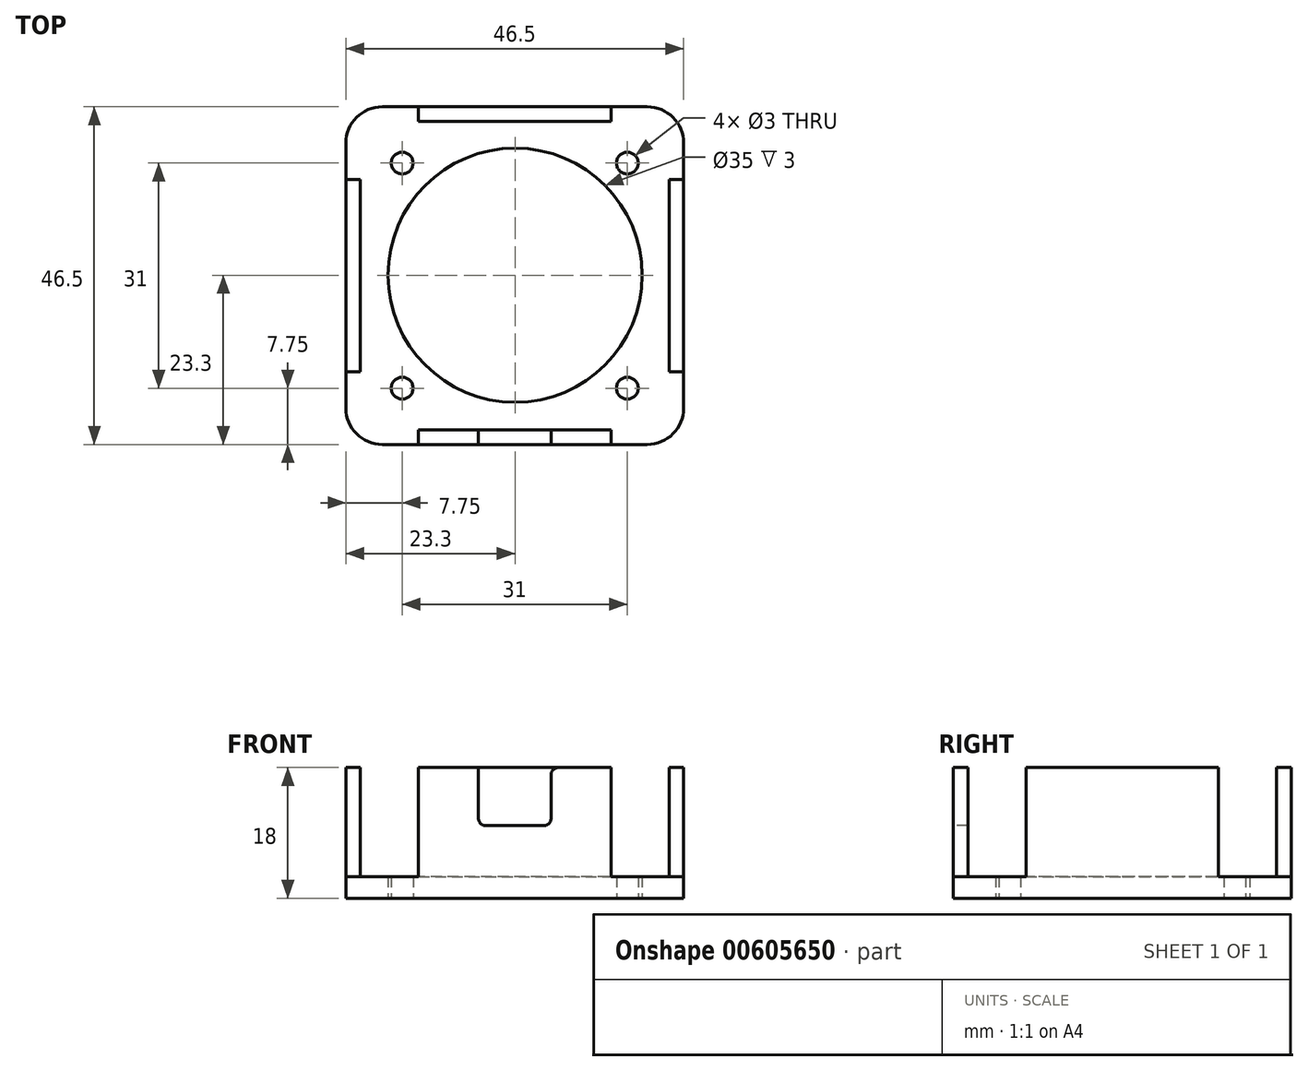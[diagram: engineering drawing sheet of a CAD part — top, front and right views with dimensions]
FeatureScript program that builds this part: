
annotation { "Feature Type Name" : "Feature", "Feature Type Description" : "" }
export const myFeature = defineFeature(function(context is Context, id is Id, definition is map)
    precondition{}
    {
        {
            var Q0;
            Q0=qCreatedBy(makeId("Top.planeOp"),FACE);
            var sketch = newSketch(context, id + "F0", { "sketchPlane" : qUnion([Q0])});
            skLineSegment(sketch, "E0.bottom", {"start": v(0, 0) * mm, "end": v(46.5, 0) * mm});
            skLineSegment(sketch, "E0.top", {"start": v(0, 46.5) * mm, "end": v(46.5, 46.5) * mm});
            skLineSegment(sketch, "E0.left", {"start": v(0, 0) * mm, "end": v(0, 46.5) * mm});
            skLineSegment(sketch, "E0.right", {"start": v(46.5, 0) * mm, "end": v(46.5, 46.5) * mm});
            skCircle(sketch, "E1", {"center": v(23.3, 23.3) * mm, "radius": 17.5 * mm});
            skCircle(sketch, "E2", {"center": v(7.75, 7.75) * mm, "radius": 1.5 * mm});
            skCircle(sketch, "E3", {"center": v(7.75, 38.75) * mm, "radius": 1.5 * mm});
            skCircle(sketch, "E4", {"center": v(38.75, 38.75) * mm, "radius": 1.5 * mm});
            skCircle(sketch, "E5", {"center": v(38.75, 7.75) * mm, "radius": 1.5 * mm});
            skSolve(sketch);
        }
        {
            var Q0;
            Q0 = qSketchRegion(id + "F0", true);
            extrude(context, id + "F1", {"entities" : qUnion([Q0]), "depth" : 3 * mm, "offsetDistance" : 25 * mm});
        }
        {
            var Q0;
            Q0=makeQuery(id+"F1.opExtrude","CAP_FACE",FACE,{"disambiguationData":[OSD([sQuery(id+"F0.wireOp",EDGE,"E0.bottom"),sQuery(id+"F0.wireOp",EDGE,"E0.top"),sQuery(id+"F0.wireOp",EDGE,"E0.left"),sQuery(id+"F0.wireOp",EDGE,"E0.right"),sQuery(id+"F0.wireOp",EDGE,"E1")])],"isStart":false});
            var sketch = newSketch(context, id + "F2", { "sketchPlane" : qUnion([Q0])});
            skLineSegment(sketch, "E6.bottom", {"start": v(0, 46.5) * mm, "end": v(2, 46.5) * mm});
            skLineSegment(sketch, "E6.top", {"start": v(0, 0) * mm, "end": v(2, 0) * mm});
            skLineSegment(sketch, "E6.left", {"start": v(0, 46.5) * mm, "end": v(0, 0) * mm});
            skLineSegment(sketch, "E6.right", {"start": v(2, 46.5) * mm, "end": v(2, 0) * mm});
            skLineSegment(sketch, "E7.bottom", {"start": v(44.5, 46.5) * mm, "end": v(46.5, 46.5) * mm});
            skLineSegment(sketch, "E7.top", {"start": v(44.5, 0) * mm, "end": v(46.5, 0) * mm});
            skLineSegment(sketch, "E7.left", {"start": v(44.5, 46.5) * mm, "end": v(44.5, 0) * mm});
            skLineSegment(sketch, "E7.right", {"start": v(46.5, 46.5) * mm, "end": v(46.5, 0) * mm});
            skLineSegment(sketch, "E8.bottom", {"start": v(2, 46.5) * mm, "end": v(44.5, 46.5) * mm});
            skLineSegment(sketch, "E8.top", {"start": v(2, 44.5) * mm, "end": v(44.5, 44.5) * mm});
            skLineSegment(sketch, "E8.left", {"start": v(2, 46.5) * mm, "end": v(2, 44.5) * mm});
            skLineSegment(sketch, "E8.right", {"start": v(44.5, 46.5) * mm, "end": v(44.5, 44.5) * mm});
            skLineSegment(sketch, "E9.bottom", {"start": v(2, 0) * mm, "end": v(44.5, 0) * mm});
            skLineSegment(sketch, "E9.top", {"start": v(2, 2) * mm, "end": v(44.5, 2) * mm});
            skLineSegment(sketch, "E9.left", {"start": v(2, 0) * mm, "end": v(2, 2) * mm});
            skLineSegment(sketch, "E9.right", {"start": v(44.5, 0) * mm, "end": v(44.5, 2) * mm});
            skSolve(sketch);
        }
        {
            var Q0;
            Q0 = qSketchRegion(id + "F2", true);
            extrude(context, id + "F3", {"entities" : qUnion([Q0]), "operationType" : NewBodyOperationType.ADD, "depth" : 15 * mm, "offsetDistance" : 25 * mm});
        }
        {
            var Q0;
            Q0=makeQuery(id+"F3.boolean.opBoolean","MERGE",FACE,{"derivedFrom":[makeQuery(id+"F1.opExtrude","SWEPT_FACE",FACE,{"disambiguationData":[OSD([sQuery(id+"F0.wireOp",EDGE,"E0.bottom")])]}),makeQuery(id+"F3.opExtrude","SWEPT_FACE",FACE,{"disambiguationData":[OSD([sQuery(id+"F2.wireOp",EDGE,"E6.top"),sQuery(id+"F2.wireOp",EDGE,"E7.top"),sQuery(id+"F2.wireOp",EDGE,"E9.bottom")])]})]});
            var sketch = newSketch(context, id + "F4", { "sketchPlane" : qUnion([Q0])});
            skLineSegment(sketch, "E10.bottom", {"start": v(10, 18) * mm, "end": v(0, 18) * mm});
            skLineSegment(sketch, "E10.top", {"start": v(10, 3) * mm, "end": v(0, 3) * mm});
            skLineSegment(sketch, "E10.left", {"start": v(10, 18) * mm, "end": v(10, 3) * mm});
            skLineSegment(sketch, "E10.right", {"start": v(0, 18) * mm, "end": v(0, 3) * mm});
            skSolve(sketch);
        }
        {
            var Q0;
            Q0 = qSketchRegion(id + "F4", true);
            extrude(context, id + "F5", {"entities" : qUnion([Q0]), "operationType" : NewBodyOperationType.REMOVE, "oppositeDirection" : true, "depth" : 10 * mm, "offsetDistance" : 25 * mm});
        }
        {
            var Q0;
            Q0=makeQuery(id+"F3.boolean.opBoolean","MERGE",FACE,{"derivedFrom":[makeQuery(id+"F1.opExtrude","SWEPT_FACE",FACE,{"disambiguationData":[OSD([sQuery(id+"F0.wireOp",EDGE,"E0.top")])]}),makeQuery(id+"F3.opExtrude","SWEPT_FACE",FACE,{"disambiguationData":[OSD([sQuery(id+"F2.wireOp",EDGE,"E6.bottom"),sQuery(id+"F2.wireOp",EDGE,"E7.bottom"),sQuery(id+"F2.wireOp",EDGE,"E8.bottom")])]})]});
            var sketch = newSketch(context, id + "F6", { "sketchPlane" : qUnion([Q0])});
            skLineSegment(sketch, "E11.bottom", {"start": v(0, 18) * mm, "end": v(-10, 18) * mm});
            skLineSegment(sketch, "E11.top", {"start": v(0, 3) * mm, "end": v(-10, 3) * mm});
            skLineSegment(sketch, "E11.left", {"start": v(0, 18) * mm, "end": v(0, 3) * mm});
            skLineSegment(sketch, "E11.right", {"start": v(-10, 18) * mm, "end": v(-10, 3) * mm});
            skSolve(sketch);
        }
        {
            var Q0;
            Q0 = qSketchRegion(id + "F6", true);
            extrude(context, id + "F7", {"entities" : qUnion([Q0]), "operationType" : NewBodyOperationType.REMOVE, "oppositeDirection" : true, "depth" : 10 * mm, "offsetDistance" : 25 * mm});
        }
        {
            var Q0;
            Q0=makeQuery(id+"F3.boolean.opBoolean","MERGE",FACE,{"derivedFrom":[makeQuery(id+"F1.opExtrude","SWEPT_FACE",FACE,{"disambiguationData":[OSD([sQuery(id+"F0.wireOp",EDGE,"E0.top")])]}),makeQuery(id+"F3.opExtrude","SWEPT_FACE",FACE,{"disambiguationData":[OSD([sQuery(id+"F2.wireOp",EDGE,"E6.bottom"),sQuery(id+"F2.wireOp",EDGE,"E7.bottom"),sQuery(id+"F2.wireOp",EDGE,"E8.bottom")])]})]});
            var sketch = newSketch(context, id + "F8", { "sketchPlane" : qUnion([Q0])});
            skLineSegment(sketch, "E12.bottom", {"start": v(-36.5, 18) * mm, "end": v(-46.5, 18) * mm});
            skLineSegment(sketch, "E12.top", {"start": v(-36.5, 3) * mm, "end": v(-46.5, 3) * mm});
            skLineSegment(sketch, "E12.left", {"start": v(-36.5, 18) * mm, "end": v(-36.5, 3) * mm});
            skLineSegment(sketch, "E12.right", {"start": v(-46.5, 18) * mm, "end": v(-46.5, 3) * mm});
            skSolve(sketch);
        }
        {
            var Q0;
            Q0 = qSketchRegion(id + "F8", true);
            extrude(context, id + "F9", {"entities" : qUnion([Q0]), "operationType" : NewBodyOperationType.REMOVE, "oppositeDirection" : true, "depth" : 10 * mm, "offsetDistance" : 25 * mm});
        }
        {
            var Q0;
            Q0=makeQuery(id+"F3.boolean.opBoolean","MERGE",FACE,{"derivedFrom":[makeQuery(id+"F1.opExtrude","SWEPT_FACE",FACE,{"disambiguationData":[OSD([sQuery(id+"F0.wireOp",EDGE,"E0.bottom")])]}),makeQuery(id+"F3.opExtrude","SWEPT_FACE",FACE,{"disambiguationData":[OSD([sQuery(id+"F2.wireOp",EDGE,"E6.top"),sQuery(id+"F2.wireOp",EDGE,"E7.top"),sQuery(id+"F2.wireOp",EDGE,"E9.bottom")])]})]});
            var sketch = newSketch(context, id + "F10", { "sketchPlane" : qUnion([Q0])});
            skLineSegment(sketch, "E13.bottom", {"start": v(46.5, 18) * mm, "end": v(36.5, 18) * mm});
            skLineSegment(sketch, "E13.top", {"start": v(46.5, 3) * mm, "end": v(36.5, 3) * mm});
            skLineSegment(sketch, "E13.left", {"start": v(46.5, 18) * mm, "end": v(46.5, 3) * mm});
            skLineSegment(sketch, "E13.right", {"start": v(36.5, 18) * mm, "end": v(36.5, 3) * mm});
            skSolve(sketch);
        }
        {
            var Q0;
            Q0 = qSketchRegion(id + "F10", true);
            extrude(context, id + "F11", {"entities" : qUnion([Q0]), "operationType" : NewBodyOperationType.REMOVE, "oppositeDirection" : true, "depth" : 10 * mm, "offsetDistance" : 25 * mm});
        }
        {
            var Q0;
            Q0=makeQuery(id+"F3.boolean.opBoolean","MERGE",EDGE,{"derivedFrom":[makeQuery(id+"F1.opExtrude","SWEPT_EDGE",EDGE,{"disambiguationData":[OSD([sQuery(id+"F0.wireOp",EDGE,"E0.top"),sQuery(id+"F0.wireOp",EDGE,"E0.right")])]}),makeQuery(id+"F3.opExtrude","SWEPT_EDGE",EDGE,{"disambiguationData":[OSD([sQuery(id+"F2.wireOp",EDGE,"E7.bottom"),sQuery(id+"F2.wireOp",EDGE,"E7.right")])]})]});
            fillet(context, id + "F12", {"entities" : qUnion([Q0]), "radius" : 5 * mm, "tangentPropagation" : true, "allowEdgeOverflow" : false});
        }
        {
            var Q0;
            Q0=makeQuery(id+"F3.boolean.opBoolean","MERGE",EDGE,{"derivedFrom":[makeQuery(id+"F1.opExtrude","SWEPT_EDGE",EDGE,{"disambiguationData":[OSD([sQuery(id+"F0.wireOp",EDGE,"E0.top"),sQuery(id+"F0.wireOp",EDGE,"E0.left")])]}),makeQuery(id+"F3.opExtrude","SWEPT_EDGE",EDGE,{"disambiguationData":[OSD([sQuery(id+"F2.wireOp",EDGE,"E6.bottom"),sQuery(id+"F2.wireOp",EDGE,"E6.left")])]})]});
            fillet(context, id + "F13", {"entities" : qUnion([Q0]), "radius" : 5 * mm, "tangentPropagation" : true, "allowEdgeOverflow" : false});
        }
        {
            var Q0;
            Q0=makeQuery(id+"F3.boolean.opBoolean","MERGE",EDGE,{"derivedFrom":[makeQuery(id+"F1.opExtrude","SWEPT_EDGE",EDGE,{"disambiguationData":[OSD([sQuery(id+"F0.wireOp",EDGE,"E0.bottom"),sQuery(id+"F0.wireOp",EDGE,"E0.right")])]}),makeQuery(id+"F3.opExtrude","SWEPT_EDGE",EDGE,{"disambiguationData":[OSD([sQuery(id+"F2.wireOp",EDGE,"E7.top"),sQuery(id+"F2.wireOp",EDGE,"E7.right")])]})]});
            fillet(context, id + "F14", {"entities" : qUnion([Q0]), "radius" : 5 * mm, "tangentPropagation" : true, "allowEdgeOverflow" : false});
        }
        {
            var Q0;
            Q0=makeQuery(id+"F3.boolean.opBoolean","MERGE",EDGE,{"derivedFrom":[makeQuery(id+"F1.opExtrude","SWEPT_EDGE",EDGE,{"disambiguationData":[OSD([sQuery(id+"F0.wireOp",EDGE,"E0.bottom"),sQuery(id+"F0.wireOp",EDGE,"E0.left")])]}),makeQuery(id+"F3.opExtrude","SWEPT_EDGE",EDGE,{"disambiguationData":[OSD([sQuery(id+"F2.wireOp",EDGE,"E6.top"),sQuery(id+"F2.wireOp",EDGE,"E6.left")])]})]});
            fillet(context, id + "F15", {"entities" : qUnion([Q0]), "radius" : 5 * mm, "tangentPropagation" : true, "allowEdgeOverflow" : false});
        }
        {
            var Q0;
            Q0=makeQuery(id+"F3.boolean.opBoolean","MERGE",FACE,{"derivedFrom":[makeQuery(id+"F1.opExtrude","SWEPT_FACE",FACE,{"disambiguationData":[OSD([sQuery(id+"F0.wireOp",EDGE,"E0.bottom")])]}),makeQuery(id+"F3.opExtrude","SWEPT_FACE",FACE,{"disambiguationData":[OSD([sQuery(id+"F2.wireOp",EDGE,"E6.top"),sQuery(id+"F2.wireOp",EDGE,"E7.top"),sQuery(id+"F2.wireOp",EDGE,"E9.bottom")])]})]});
            var sketch = newSketch(context, id + "F16", { "sketchPlane" : qUnion([Q0])});
            skLineSegment(sketch, "E14.bottom", {"start": v(18.25, 18) * mm, "end": v(28.25, 18) * mm});
            skLineSegment(sketch, "E14.top", {"start": v(18.25, 10) * mm, "end": v(28.25, 10) * mm});
            skLineSegment(sketch, "E14.left", {"start": v(18.25, 18) * mm, "end": v(18.25, 10) * mm});
            skLineSegment(sketch, "E14.right", {"start": v(28.25, 18) * mm, "end": v(28.25, 10) * mm});
            skSolve(sketch);
        }
        {
            var Q0;
            Q0 = qSketchRegion(id + "F16", true);
            extrude(context, id + "F17", {"entities" : qUnion([Q0]), "operationType" : NewBodyOperationType.REMOVE, "oppositeDirection" : true, "depth" : 25 * mm, "offsetDistance" : 25 * mm});
        }
        {
            var Q0;
            Q0=makeQuery(id+"F17.boolean.opBoolean","COPY",EDGE,{"derivedFrom":makeQuery(id+"F17.opExtrude","SWEPT_EDGE",EDGE,{"disambiguationData":[OSD([sQuery(id+"F16.wireOp",EDGE,"E14.top"),sQuery(id+"F16.wireOp",EDGE,"E14.right")])]})});
            var Q1;
            Q1=makeQuery(id+"F17.boolean.opBoolean","COPY",EDGE,{"derivedFrom":makeQuery(id+"F17.opExtrude","SWEPT_EDGE",EDGE,{"disambiguationData":[OSD([sQuery(id+"F16.wireOp",EDGE,"E14.top"),sQuery(id+"F16.wireOp",EDGE,"E14.left")])]})});
            fillet(context, id + "F18", {"entities" : qUnion([Q0, Q1]), "radius" : 1 * mm, "tangentPropagation" : true, "allowEdgeOverflow" : false});
        }
        {
            var Q0;
            Q0=makeQuery(id+"F17.boolean.opBoolean","COPY",EDGE,{"derivedFrom":makeQuery(id+"F17.opExtrude","SWEPT_EDGE",EDGE,{"disambiguationData":[OSD([sQuery(id+"F2.wireOp",EDGE,"E6.top"),sQuery(id+"F2.wireOp",EDGE,"E7.top"),sQuery(id+"F2.wireOp",EDGE,"E9.bottom"),sQuery(id+"F16.wireOp",EDGE,"E14.bottom"),sQuery(id+"F16.wireOp",EDGE,"E14.left")])]})});
            var Q1;
            Q1=makeQuery(id+"F17.boolean.opBoolean","COPY",EDGE,{"derivedFrom":makeQuery(id+"F17.opExtrude","SWEPT_EDGE",EDGE,{"disambiguationData":[OSD([sQuery(id+"F2.wireOp",EDGE,"E6.top"),sQuery(id+"F2.wireOp",EDGE,"E7.top"),sQuery(id+"F2.wireOp",EDGE,"E9.bottom"),sQuery(id+"F16.wireOp",EDGE,"E14.bottom"),sQuery(id+"F16.wireOp",EDGE,"E14.right")])]})});
            fillet(context, id + "F19", {"entities" : qUnion([Q0, Q1]), "radius" : 1 * mm, "tangentPropagation" : true, "allowEdgeOverflow" : false});
        }
    });
